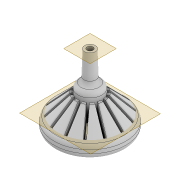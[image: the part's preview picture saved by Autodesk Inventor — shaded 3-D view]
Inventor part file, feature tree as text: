
AUTODESK INVENTOR PART (.ipt)
format: ipt  version: 2022 (Build 260153000, 153)  size: 354,816 bytes
history: native  units: mm
features: sketch x7, extrude x5, fillet x3, plane x2, chamfer x1, loft x1, projected_geometry x1
ambient origin geometry x8: Origin, YZ Plane, XZ Plane, XY Plane, X Axis, Y Axis, Z Axis, Center Point
bodies: Body1 (feature_tree)
feature tree (20):
  extrude  "Extrusion11"  Depth=3.0mm TaperAngle=0.0deg
  extrude  "Extrusion12"  Depth=3.0mm TaperAngle=0.0deg
  extrude  "Extrusion13"  Depth=1.0mm
  plane  "Work Plane7"
  extrude  "Extrusion14"  Depth=25.0mm TaperAngle=0.0deg
  chamfer  "Chamfer1"  Distance=22.0mm
  sketch  "Sketch21"  dims[d96=10.0mm]
  plane  "Work Plane8"
  loft  "Loft3"
  extrude  "Extrusion15"  Depth=3.0mm
  fillet  "Fillet3"  Radius=25.0mm
  fillet  "Fillet4"  Radius=9.0mm
  fillet  "Fillet5"  [1 undecoded]
  sketch  "Sketch16"  dims[d82=60.0mm d83=3.0mm d84=0.0mm]
  sketch  "Sketch17"  dims[d85=3.0mm d86=25.0mm d87=0.0mm]
  projected_geometry  "Projected Loop3"
  sketch  "Sketch18"  dims[d88=1.0mm d89=1.0mm]
  sketch  "Sketch20"  dims[d90=70.0mm d92=360.0deg d94=25.0mm d95=0.0mm]
  sketch  "Sketch22"  dims[d97=20.0mm]
  sketch  "Sketch23"  dims[d98=5.0mm d99=22.0mm d100=0.0mm d101=18.0mm d102=2.0mm d103=45.0deg d104=10.3mm d105=25.0mm d106=9.0mm d107=0.0mm d108=90.0deg d109=0.0mm d110=90.0deg d111=5.0mm d112=35.0mm d113=0.0mm d114=5.0mm d115=5.0mm d116=3.0mm]
note: 1 required parameter value undecoded (feature->parameter linkage not recoverable at this tier; creation-order binding heuristic only, values carry confidence <= 0.55)
